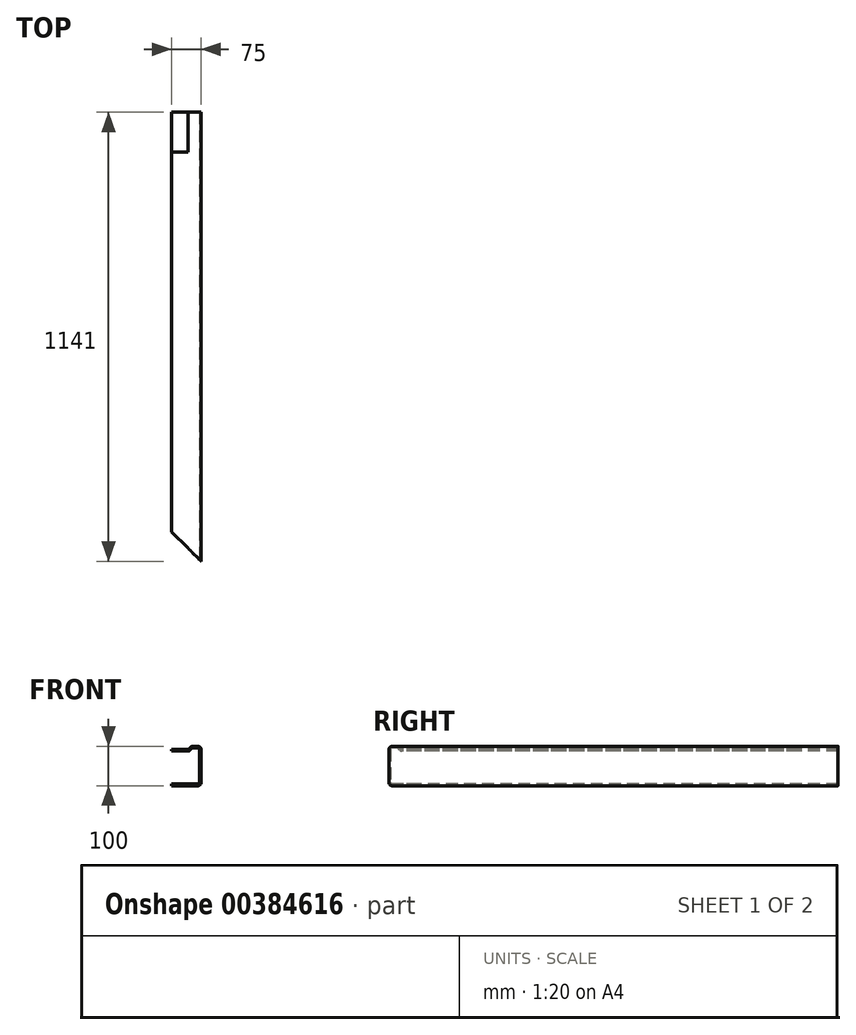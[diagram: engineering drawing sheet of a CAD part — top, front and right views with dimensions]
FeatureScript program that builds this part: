
annotation { "Feature Type Name" : "Feature", "Feature Type Description" : "" }
export const myFeature = defineFeature(function(context is Context, id is Id, definition is map)
    precondition{}
    {
        {
            var Q0;
            Q0=qCreatedBy(makeId("Front.planeOp"),FACE);
            var sketch = newSketch(context, id + "F0", { "sketchPlane" : qUnion([Q0])});
            skLineSegment(sketch, "E0.bottom", {"start": v(-29.5, -50) * mm, "end": v(37.5, -50) * mm});
            skLineSegment(sketch, "E0.top", {"start": v(-29.5, 50) * mm, "end": v(-16.23, 50) * mm});
            skLineSegment(sketch, "E0.left", {"start": v(-37.5, -42) * mm, "end": v(-37.5, 42) * mm});
            skPoint(sketch, "E0.middle", {"position": v(0, 0) * mm});
            skLineSegment(sketch, "E1", {"start": v(-10.1, 47.14) * mm, "end": v(-6.99, 43.43) * mm});
            skLineSegment(sketch, "E2", {"start": v(-3.92, 42) * mm, "end": v(37.5, 42) * mm});
            skLineSegment(sketch, "E3", {"start": v(-3.92, 38) * mm, "end": v(37.5, 38) * mm});
            skPoint(sketch, "E4.orphan", {"position": v(37.5, 50) * mm});
            skPoint(sketch, "E5.orphan", {"position": v(35.5, 48) * mm});
            skLineSegment(sketch, "E6.0", {"start": v(-13.17, 44.57) * mm, "end": v(-10.05, 40.86) * mm});
            skLineSegment(sketch, "E7.0", {"start": v(-29.5, -46) * mm, "end": v(37.5, -46) * mm});
            skLineSegment(sketch, "E8.0", {"start": v(-33.5, -42) * mm, "end": v(-33.5, 42) * mm});
            skLineSegment(sketch, "E9.0", {"start": v(-29.5, 46) * mm, "end": v(-16.23, 46) * mm});
            skPoint(sketch, "E10.orphan", {"position": v(-35.5, 48) * mm});
            skPoint(sketch, "E11.orphan", {"position": v(-35.5, -48) * mm});
            skLineSegment(sketch, "E12", {"start": v(37.5, 42) * mm, "end": v(37.5, 38) * mm});
            skLineSegment(sketch, "E13", {"start": v(37.5, -46) * mm, "end": v(37.5, -50) * mm});
            skPoint(sketch, "E14.visualSharp", {"position": v(-37.5, 50) * mm});
            skArc(sketch, "E14.filletArc", {"start": v(-29.5, 50) * mm, "mid": v(-35.16, 47.66) * mm, "end": v(-37.5, 42) * mm});
            skPoint(sketch, "E15.visualSharp", {"position": v(-33.5, 46) * mm});
            skArc(sketch, "E15.filletArc", {"start": v(-29.5, 46) * mm, "mid": v(-32.33, 44.83) * mm, "end": v(-33.5, 42) * mm});
            skPoint(sketch, "E16.visualSharp", {"position": v(-14.37, 46) * mm});
            skArc(sketch, "E16.filletArc", {"start": v(-13.17, 44.57) * mm, "mid": v(-14.54, 45.63) * mm, "end": v(-16.23, 46) * mm});
            skPoint(sketch, "E17.visualSharp", {"position": v(-12.5, 50) * mm});
            skArc(sketch, "E17.filletArc", {"start": v(-10.1, 47.14) * mm, "mid": v(-12.85, 49.25) * mm, "end": v(-16.23, 50) * mm});
            skPoint(sketch, "E18.visualSharp", {"position": v(-7.65, 38) * mm});
            skArc(sketch, "E18.filletArc", {"start": v(-10.05, 40.86) * mm, "mid": v(-7.3, 38.75) * mm, "end": v(-3.92, 38) * mm});
            skPoint(sketch, "E19.visualSharp", {"position": v(-5.79, 42) * mm});
            skArc(sketch, "E19.filletArc", {"start": v(-6.99, 43.43) * mm, "mid": v(-5.61, 42.37) * mm, "end": v(-3.92, 42) * mm});
            skPoint(sketch, "E20.visualSharp", {"position": v(-33.5, -46) * mm});
            skArc(sketch, "E20.filletArc", {"start": v(-33.5, -42) * mm, "mid": v(-32.33, -44.83) * mm, "end": v(-29.5, -46) * mm});
            skPoint(sketch, "E21.visualSharp", {"position": v(-37.5, -50) * mm});
            skArc(sketch, "E21.filletArc", {"start": v(-37.5, -42) * mm, "mid": v(-35.16, -47.66) * mm, "end": v(-29.5, -50) * mm});
            skSolve(sketch);
        }
        {
            var Q0;
            Q0=makeQuery(id+"F0.imprint","IMPRINT",FACE,{"disambiguationData":[TD([[makeQuery(id+"F0.imprint","IMPRINT",EDGE,{"derivedFrom":sQuery(id+"F0.wireOp",EDGE,"E0.bottom")}),1.0]])]});
            extrude(context, id + "F1", {"entities" : qUnion([Q0]), "oppositeDirection" : true, "depth" : 1141 * mm});
        }
        {
            var Q0;
            Q0=qCreatedBy(makeId("Top.planeOp"),FACE);
            var sketch = newSketch(context, id + "F2", { "sketchPlane" : qUnion([Q0])});
            skLineSegment(sketch, "E22", {"start": v(0, 0) * mm, "end": v(-37.5, 0) * mm});
            skLineSegment(sketch, "E23", {"start": v(0, 0) * mm, "end": v(37.5, 0) * mm});
            skLineSegment(sketch, "E24", {"start": v(37.5, 0) * mm, "end": v(37.5, 75) * mm});
            skLineSegment(sketch, "E25", {"start": v(37.5, 75) * mm, "end": v(-37.5, 0) * mm});
            skSolve(sketch);
        }
        {
            var Q0;
            Q0=sQuery(id+"F0.wireOp",EDGE,"E0.left");
            var Q1;
            Q1=sQuery(id+"F2.wireOp",EDGE,"E25");
            cPlane(context, id + "F3", {"entities" : qUnion([Q0, Q1]), "cplaneType" : CPlaneType.LINE_ANGLE, "offset" : 25 * mm, "angle" : 0 * degree, "width" : 150 * mm, "height" : 150 * mm});
        }
        {
            var Q0;
            Q0=qCreatedBy(id+"F3.planeOp",FACE);
            var sketch = newSketch(context, id + "F4", { "sketchPlane" : qUnion([Q0])});
            skLineSegment(sketch, "E26.bottom", {"start": v(-175, -75) * mm, "end": v(175, -75) * mm});
            skLineSegment(sketch, "E26.top", {"start": v(-175, 75) * mm, "end": v(175, 75) * mm});
            skLineSegment(sketch, "E26.left", {"start": v(-175, -75) * mm, "end": v(-175, 75) * mm});
            skLineSegment(sketch, "E26.right", {"start": v(175, -75) * mm, "end": v(175, 75) * mm});
            skPoint(sketch, "E26.middle", {"position": v(0, 0) * mm});
            skSolve(sketch);
        }
        {
            var Q0;
            Q0=qSketchRegion(id+"F4",true);
            extrude(context, id + "F5", {"entities" : qUnion([Q0]), "operationType" : NewBodyOperationType.REMOVE, "depth" : 150 * mm});
        }
        {
            var Q0;
            Q0=qCreatedBy(makeId("Right.planeOp"),FACE);
            cPlane(context, id + "F6", {"entities" : qUnion([Q0]), "cplaneType" : CPlaneType.OFFSET, "offset" : 200 * mm, "width" : 150 * mm, "height" : 150 * mm});
        }
        {
            var Q0;
            Q0=makeQuery(id+"F1.opExtrude","SWEPT_BODY",BODY,{"disambiguationData":[OSD([sQuery(id+"F0.wireOp",EDGE,"E0.bottom"),sQuery(id+"F0.wireOp",EDGE,"E0.top"),sQuery(id+"F0.wireOp",EDGE,"E0.left"),sQuery(id+"F0.wireOp",EDGE,"E1"),sQuery(id+"F0.wireOp",EDGE,"E2"),sQuery(id+"F0.wireOp",EDGE,"E3"),sQuery(id+"F0.wireOp",EDGE,"E6.0"),sQuery(id+"F0.wireOp",EDGE,"E7.0"),sQuery(id+"F0.wireOp",EDGE,"E8.0"),sQuery(id+"F0.wireOp",EDGE,"E9.0"),sQuery(id+"F0.wireOp",EDGE,"E12"),sQuery(id+"F0.wireOp",EDGE,"E13"),sQuery(id+"F0.wireOp",EDGE,"E14.filletArc"),sQuery(id+"F0.wireOp",EDGE,"E15.filletArc"),sQuery(id+"F0.wireOp",EDGE,"E16.filletArc"),sQuery(id+"F0.wireOp",EDGE,"E17.filletArc"),sQuery(id+"F0.wireOp",EDGE,"E18.filletArc"),sQuery(id+"F0.wireOp",EDGE,"E19.filletArc"),sQuery(id+"F0.wireOp",EDGE,"E20.filletArc"),sQuery(id+"F0.wireOp",EDGE,"E21.filletArc")])]});
            var Q1;
            Q1=qCreatedBy(id+"F6.planeOp",FACE);
            mirror(context, id + "F7", {"entities" : qUnion([Q0]), "mirrorPlane" : qUnion([Q1])});
        }
        {
            var Q0;
            Q0=makeQuery(id+"F1.opExtrude","SWEPT_BODY",BODY,{"disambiguationData":[OSD([sQuery(id+"F0.wireOp",EDGE,"E0.bottom"),sQuery(id+"F0.wireOp",EDGE,"E0.top"),sQuery(id+"F0.wireOp",EDGE,"E0.left"),sQuery(id+"F0.wireOp",EDGE,"E1"),sQuery(id+"F0.wireOp",EDGE,"E2"),sQuery(id+"F0.wireOp",EDGE,"E3"),sQuery(id+"F0.wireOp",EDGE,"E6.0"),sQuery(id+"F0.wireOp",EDGE,"E7.0"),sQuery(id+"F0.wireOp",EDGE,"E8.0"),sQuery(id+"F0.wireOp",EDGE,"E9.0"),sQuery(id+"F0.wireOp",EDGE,"E12"),sQuery(id+"F0.wireOp",EDGE,"E13"),sQuery(id+"F0.wireOp",EDGE,"E14.filletArc"),sQuery(id+"F0.wireOp",EDGE,"E15.filletArc"),sQuery(id+"F0.wireOp",EDGE,"E16.filletArc"),sQuery(id+"F0.wireOp",EDGE,"E17.filletArc"),sQuery(id+"F0.wireOp",EDGE,"E18.filletArc"),sQuery(id+"F0.wireOp",EDGE,"E19.filletArc"),sQuery(id+"F0.wireOp",EDGE,"E20.filletArc"),sQuery(id+"F0.wireOp",EDGE,"E21.filletArc")])]});
            var Q1;
            Q1=qCreatedBy(id+"F6.planeOp",FACE);
            mirror(context, id + "F8", {"operationType" : NewBodyOperationType.ADD, "entities" : qUnion([Q0]), "mirrorPlane" : qUnion([Q1])});
        }
        {
            var Q0;
            Q0=qCreatedBy(id+"F6.planeOp",FACE);
            cPlane(context, id + "F9", {"entities" : qUnion([Q0]), "cplaneType" : CPlaneType.OFFSET, "offset" : 500 * mm, "width" : 150 * mm, "height" : 150 * mm});
        }
        {
            var Q0;
            Q0=makeQuery(id+"F1.opExtrude","SWEPT_BODY",BODY,{"disambiguationData":[OSD([sQuery(id+"F0.wireOp",EDGE,"E0.bottom"),sQuery(id+"F0.wireOp",EDGE,"E0.top"),sQuery(id+"F0.wireOp",EDGE,"E0.left"),sQuery(id+"F0.wireOp",EDGE,"E1"),sQuery(id+"F0.wireOp",EDGE,"E2"),sQuery(id+"F0.wireOp",EDGE,"E3"),sQuery(id+"F0.wireOp",EDGE,"E6.0"),sQuery(id+"F0.wireOp",EDGE,"E7.0"),sQuery(id+"F0.wireOp",EDGE,"E8.0"),sQuery(id+"F0.wireOp",EDGE,"E9.0"),sQuery(id+"F0.wireOp",EDGE,"E12"),sQuery(id+"F0.wireOp",EDGE,"E13"),sQuery(id+"F0.wireOp",EDGE,"E14.filletArc"),sQuery(id+"F0.wireOp",EDGE,"E15.filletArc"),sQuery(id+"F0.wireOp",EDGE,"E16.filletArc"),sQuery(id+"F0.wireOp",EDGE,"E17.filletArc"),sQuery(id+"F0.wireOp",EDGE,"E18.filletArc"),sQuery(id+"F0.wireOp",EDGE,"E19.filletArc"),sQuery(id+"F0.wireOp",EDGE,"E20.filletArc"),sQuery(id+"F0.wireOp",EDGE,"E21.filletArc")])]});
            var Q1;
            Q1=qCreatedBy(id+"F9.planeOp",FACE);
            mirror(context, id + "F10", {"entities" : qUnion([Q0]), "mirrorPlane" : qUnion([Q1])});
        }
        {
            var Q0;
            Q0=makeQuery(id+"F1.opExtrude","SWEPT_FACE",FACE,{"disambiguationData":[OSD([sQuery(id+"F0.wireOp",EDGE,"E2")])]});
            var sketch = newSketch(context, id + "F11", { "sketchPlane" : qUnion([Q0])});
            skLineSegment(sketch, "E27.bottom", {"start": v(37.5, 1141) * mm, "end": v(-3.9, 1141) * mm});
            skLineSegment(sketch, "E27.top", {"start": v(37.5, 1040) * mm, "end": v(-3.9, 1040) * mm});
            skLineSegment(sketch, "E27.left", {"start": v(37.5, 1141) * mm, "end": v(37.5, 1040) * mm});
            skLineSegment(sketch, "E27.right", {"start": v(-3.9, 1141) * mm, "end": v(-3.9, 1040) * mm});
            skSolve(sketch);
        }
        {
            var Q0;
            Q0=makeQuery(id+"F11.imprint","IMPRINT",FACE,{"disambiguationData":[TD([[makeQuery(id+"F11.imprint","IMPRINT",EDGE,{"derivedFrom":sQuery(id+"F11.wireOp",EDGE,"E27.bottom")}),-1.0]])]});
            extrude(context, id + "F12", {"entities" : qUnion([Q0]), "operationType" : NewBodyOperationType.REMOVE, "oppositeDirection" : true, "depth" : 4 * mm});
        }
        {
            var Q0;
            Q0=makeQuery(id+"F1.opExtrude","SWEPT_BODY",BODY,{"disambiguationData":[OSD([sQuery(id+"F0.wireOp",EDGE,"E0.bottom"),sQuery(id+"F0.wireOp",EDGE,"E0.top"),sQuery(id+"F0.wireOp",EDGE,"E0.left"),sQuery(id+"F0.wireOp",EDGE,"E1"),sQuery(id+"F0.wireOp",EDGE,"E2"),sQuery(id+"F0.wireOp",EDGE,"E3"),sQuery(id+"F0.wireOp",EDGE,"E6.0"),sQuery(id+"F0.wireOp",EDGE,"E7.0"),sQuery(id+"F0.wireOp",EDGE,"E8.0"),sQuery(id+"F0.wireOp",EDGE,"E9.0"),sQuery(id+"F0.wireOp",EDGE,"E12"),sQuery(id+"F0.wireOp",EDGE,"E13"),sQuery(id+"F0.wireOp",EDGE,"E14.filletArc"),sQuery(id+"F0.wireOp",EDGE,"E15.filletArc"),sQuery(id+"F0.wireOp",EDGE,"E16.filletArc"),sQuery(id+"F0.wireOp",EDGE,"E17.filletArc"),sQuery(id+"F0.wireOp",EDGE,"E18.filletArc"),sQuery(id+"F0.wireOp",EDGE,"E19.filletArc"),sQuery(id+"F0.wireOp",EDGE,"E20.filletArc"),sQuery(id+"F0.wireOp",EDGE,"E21.filletArc")])]});
            var Q1;
            Q1=qCreatedBy(id+"F6.planeOp",FACE);
            mirror(context, id + "F13", {"operationType" : NewBodyOperationType.INTERSECT, "entities" : qUnion([Q0]), "mirrorPlane" : qUnion([Q1])});
        }
    });
